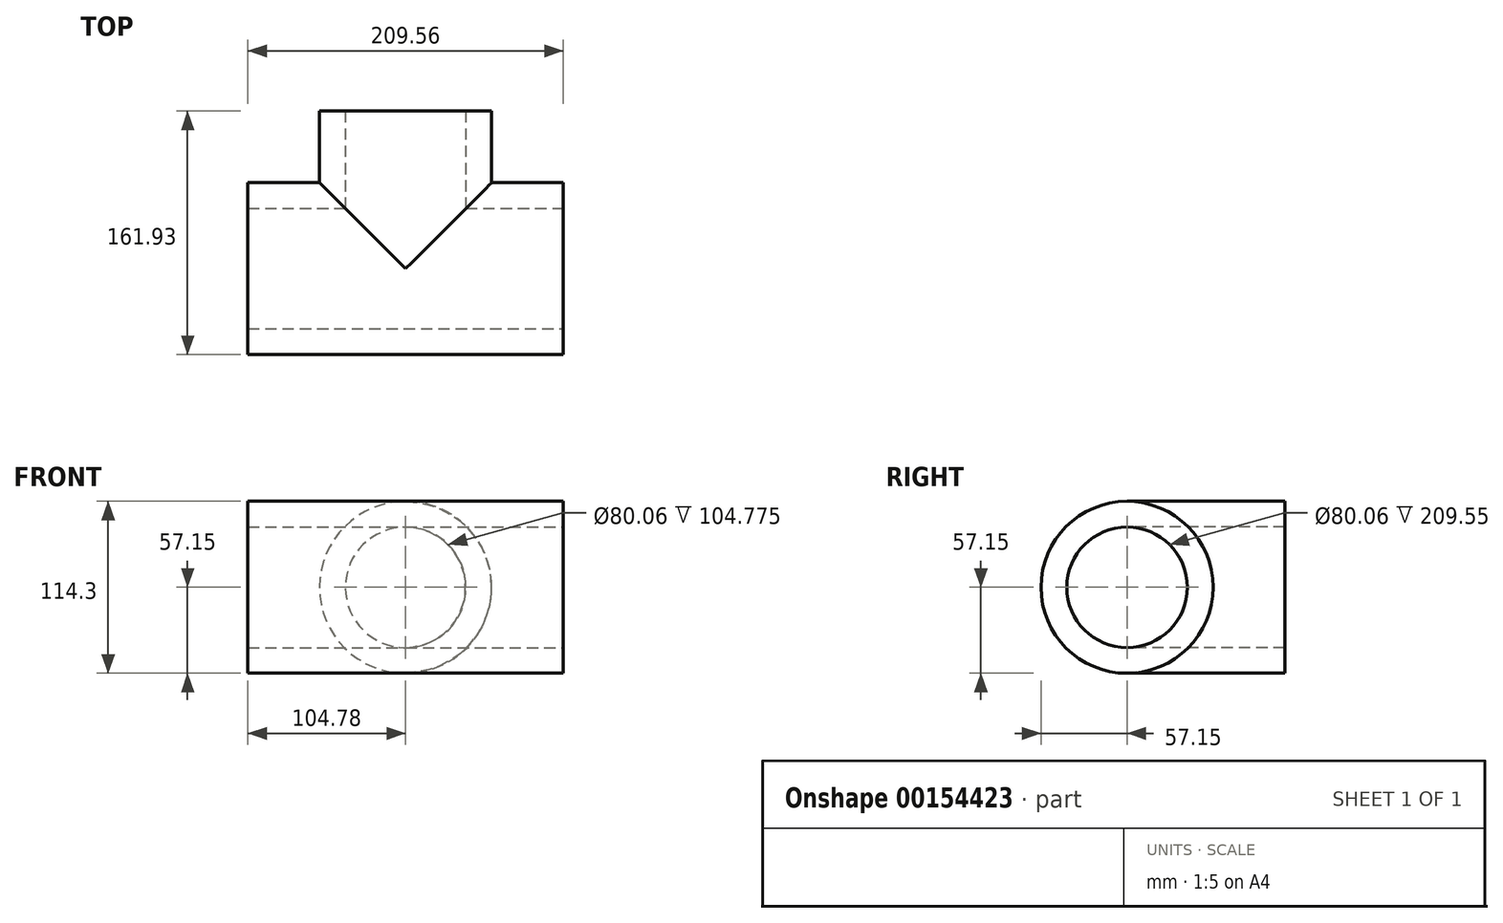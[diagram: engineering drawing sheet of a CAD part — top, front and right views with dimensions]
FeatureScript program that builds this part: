
annotation { "Feature Type Name" : "Feature", "Feature Type Description" : "" }
export const myFeature = defineFeature(function(context is Context, id is Id, definition is map)
    precondition{}
    {
        {
            var Q0;
            Q0=qCreatedBy(makeId("Front.planeOp"),FACE);
            var sketch = newSketch(context, id + "F0", { "sketchPlane" : qUnion([Q0])});
            skCircle(sketch, "E0", {"center": v(0, 0) * mm, "radius": 57.15 * mm});
            skSolve(sketch);
        }
        {
            var Q0;
            Q0=qCreatedBy(makeId("Front.planeOp"),FACE);
            var sketch = newSketch(context, id + "F1", { "sketchPlane" : qUnion([Q0])});
            skCircle(sketch, "E1.0", {"center": v(0, 0) * mm, "radius": 40.03 * mm});
            skSolve(sketch);
        }
        {
            var Q0;
            Q0=qCreatedBy(makeId("Right.planeOp"),FACE);
            var sketch = newSketch(context, id + "F2", { "sketchPlane" : qUnion([Q0])});
            skCircle(sketch, "E2", {"center": v(0, 0) * mm, "radius": 57.15 * mm});
            skSolve(sketch);
        }
        {
            var Q0;
            Q0=makeQuery(id+"F2.imprint","IMPRINT",FACE,{"disambiguationData":[TD([[makeQuery(id+"F2.imprint","IMPRINT",EDGE,{"derivedFrom":sQuery(id+"F2.wireOp",EDGE,"E2")}),1.0]])]});
            extrude(context, id + "F3", {"entities" : qUnion([Q0]), "depth" : 104.77 * mm, "hasSecondDirection" : true, "secondDirectionOppositeDirection" : true, "secondDirectionDepth" : 104.77 * mm});
        }
        {
            var Q0;
            Q0 = qSketchRegion(id + "F0", true);
            extrude(context, id + "F4", {"entities" : qUnion([Q0]), "operationType" : NewBodyOperationType.ADD, "oppositeDirection" : true, "depth" : 104.77 * mm});
        }
        {
            var Q0;
            Q0=makeQuery(id+"F3.opExtrude","CAP_FACE",FACE,{"disambiguationData":[OSD([sQuery(id+"F2.wireOp",EDGE,"E2")])],"isStart":false});
            var sketch = newSketch(context, id + "F5", { "sketchPlane" : qUnion([Q0])});
            skCircle(sketch, "E3.0", {"center": v(0, 0) * mm, "radius": 40.03 * mm});
            skSolve(sketch);
        }
        {
            var Q0;
            Q0=makeQuery(id+"F5.imprint","IMPRINT",FACE,{"disambiguationData":[TD([[makeQuery(id+"F5.imprint","IMPRINT",EDGE,{"derivedFrom":sQuery(id+"F5.wireOp",EDGE,"E3.0")}),1.0]])]});
            extrude(context, id + "F6", {"entities" : qUnion([Q0]), "operationType" : NewBodyOperationType.REMOVE, "endBound" : BoundingType.THROUGH_ALL, "oppositeDirection" : true, "depth" : 25.4 * mm});
        }
        {
            var Q0;
            Q0 = qSketchRegion(id + "F1", true);
            extrude(context, id + "F7", {"entities" : qUnion([Q0]), "operationType" : NewBodyOperationType.REMOVE, "endBound" : BoundingType.THROUGH_ALL, "oppositeDirection" : true, "depth" : 25.4 * mm});
        }
    });
